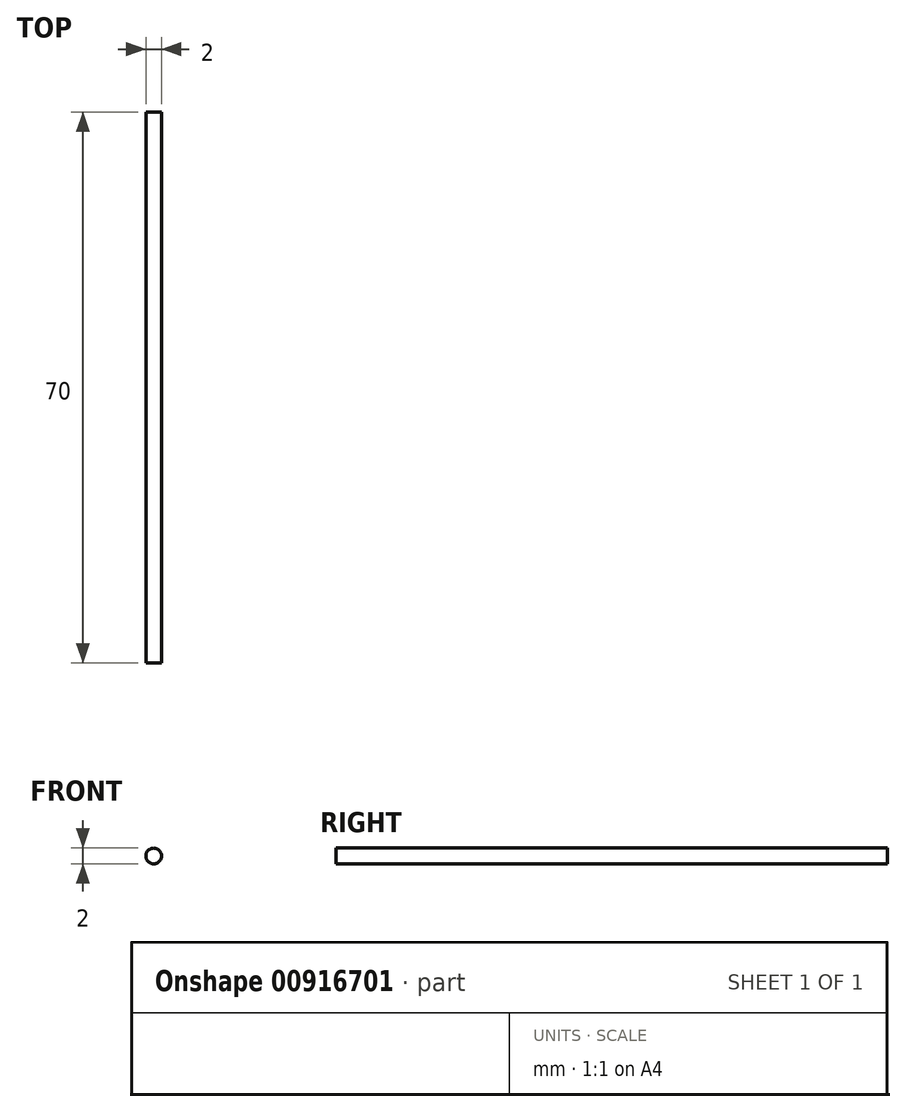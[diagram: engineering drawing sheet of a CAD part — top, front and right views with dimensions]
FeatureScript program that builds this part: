
annotation { "Feature Type Name" : "Feature", "Feature Type Description" : "" }
export const myFeature = defineFeature(function(context is Context, id is Id, definition is map)
    precondition{}
    {
        {
            var Q0;
            Q0=qCreatedBy(makeId("Front.planeOp"),FACE);
            var sketch = newSketch(context, id + "F0", { "sketchPlane" : qUnion([Q0])});
            skCircle(sketch, "E0", {"center": v(0, 0) * mm, "radius": 1 * mm});
            skSolve(sketch);
        }
        {
            var Q0;
            Q0=qCreatedBy(makeId("Top.planeOp"),FACE);
            var sketch = newSketch(context, id + "F1", { "sketchPlane" : qUnion([Q0])});
            skLineSegment(sketch, "E1", {"start": v(0, 0) * mm, "end": v(0, 70) * mm});
            skSolve(sketch);
        }
        {
            var Q0;
            Q0 = qSketchRegion(id + "F0", true);
            var Q1;
            Q1 = qConstructionFilter(qBodyType(qCreatedBy(id + "F1" ,EDGE), BodyType.WIRE), ConstructionObject.NO);
            sweep(context, id + "F2", {"profiles" : qUnion([Q0]), "path" : qUnion([Q1])});
        }
    });
